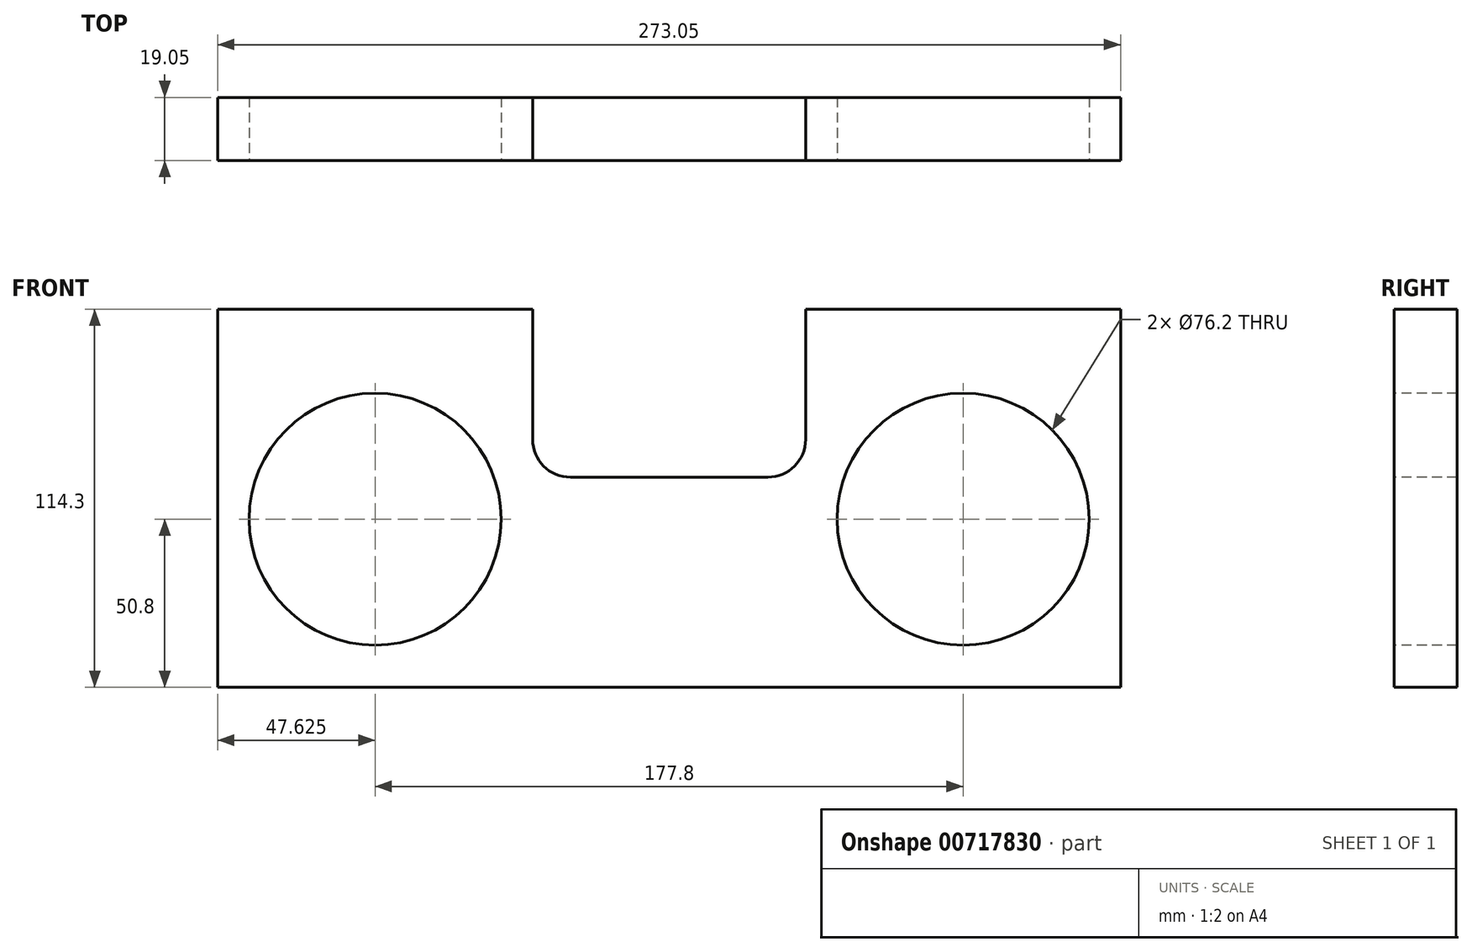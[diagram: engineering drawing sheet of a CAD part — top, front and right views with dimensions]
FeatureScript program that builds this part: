
annotation { "Feature Type Name" : "Feature", "Feature Type Description" : "" }
export const myFeature = defineFeature(function(context is Context, id is Id, definition is map)
    precondition{}
    {
        {
            var Q0;
            Q0=qCreatedBy(makeId("Front.planeOp"),FACE);
            var sketch = newSketch(context, id + "F0", { "sketchPlane" : qUnion([Q0])});
            skLineSegment(sketch, "E0.bottom", {"start": v(0, 0) * mm, "end": v(273.05, 0) * mm});
            skLineSegment(sketch, "E0.top", {"start": v(0, 114.3) * mm, "end": v(273.05, 114.3) * mm});
            skLineSegment(sketch, "E0.left", {"start": v(0, 0) * mm, "end": v(0, 114.3) * mm});
            skLineSegment(sketch, "E0.right", {"start": v(273.05, 0) * mm, "end": v(273.05, 114.3) * mm});
            skSolve(sketch);
        }
        {
            var Q0;
            Q0=makeQuery(id+"F0.imprint","IMPRINT",FACE,{"disambiguationData":[TD([[makeQuery(id+"F0.imprint","IMPRINT",EDGE,{"derivedFrom":sQuery(id+"F0.wireOp",EDGE,"E0.bottom")}),1.0]])]});
            extrude(context, id + "F1", {"entities" : qUnion([Q0]), "depth" : 19.05 * mm, "offsetDistance" : 25.4 * mm});
        }
        {
            var Q0;
            Q0=makeQuery(id+"F1.opExtrude","CAP_FACE",FACE,{"disambiguationData":[OSD([sQuery(id+"F0.wireOp",EDGE,"E0.bottom"),sQuery(id+"F0.wireOp",EDGE,"E0.top"),sQuery(id+"F0.wireOp",EDGE,"E0.left"),sQuery(id+"F0.wireOp",EDGE,"E0.right")])],"isStart":false});
            var sketch = newSketch(context, id + "F2", { "sketchPlane" : qUnion([Q0])});
            skCircle(sketch, "E1", {"center": v(47.63, 50.8) * mm, "radius": 38.1 * mm});
            skCircle(sketch, "E2", {"center": v(225.43, 50.8) * mm, "radius": 38.1 * mm});
            skSolve(sketch);
        }
        {
            var Q0;
            Q0 = qSketchRegion(id + "F2", true);
            extrude(context, id + "F3", {"entities" : qUnion([Q0]), "operationType" : NewBodyOperationType.REMOVE, "oppositeDirection" : true, "depth" : 25.4 * mm, "offsetDistance" : 25.4 * mm});
        }
        {
            var Q0;
            Q0=makeQuery(id+"F1.opExtrude","CAP_FACE",FACE,{"disambiguationData":[OSD([sQuery(id+"F0.wireOp",EDGE,"E0.bottom"),sQuery(id+"F0.wireOp",EDGE,"E0.top"),sQuery(id+"F0.wireOp",EDGE,"E0.left"),sQuery(id+"F0.wireOp",EDGE,"E0.right")])],"isStart":false});
            var sketch = newSketch(context, id + "F4", { "sketchPlane" : qUnion([Q0])});
            skLineSegment(sketch, "E3", {"start": v(95.25, 114.3) * mm, "end": v(95.25, 74.93) * mm});
            skLineSegment(sketch, "E4", {"start": v(106.68, 63.5) * mm, "end": v(166.37, 63.5) * mm});
            skLineSegment(sketch, "E5", {"start": v(177.8, 74.93) * mm, "end": v(177.8, 114.3) * mm});
            skLineSegment(sketch, "E6", {"start": v(177.8, 114.3) * mm, "end": v(95.25, 114.3) * mm});
            skPoint(sketch, "E7.visualSharp", {"position": v(95.25, 63.5) * mm});
            skArc(sketch, "E7.filletArc", {"start": v(95.25, 74.93) * mm, "mid": v(98.6, 66.85) * mm, "end": v(106.68, 63.5) * mm});
            skPoint(sketch, "E8.visualSharp", {"position": v(177.8, 63.5) * mm});
            skArc(sketch, "E8.filletArc", {"start": v(166.37, 63.5) * mm, "mid": v(174.45, 66.85) * mm, "end": v(177.8, 74.93) * mm});
            skSolve(sketch);
        }
        {
            var Q0;
            Q0=makeQuery(id+"F4.imprint","IMPRINT",FACE,{"disambiguationData":[TD([[makeQuery(id+"F4.imprint","IMPRINT",EDGE,{"derivedFrom":sQuery(id+"F4.wireOp",EDGE,"E3")}),1.0]])]});
            extrude(context, id + "F5", {"entities" : qUnion([Q0]), "operationType" : NewBodyOperationType.REMOVE, "oppositeDirection" : true, "depth" : 25.4 * mm, "offsetDistance" : 25.4 * mm});
        }
    });
